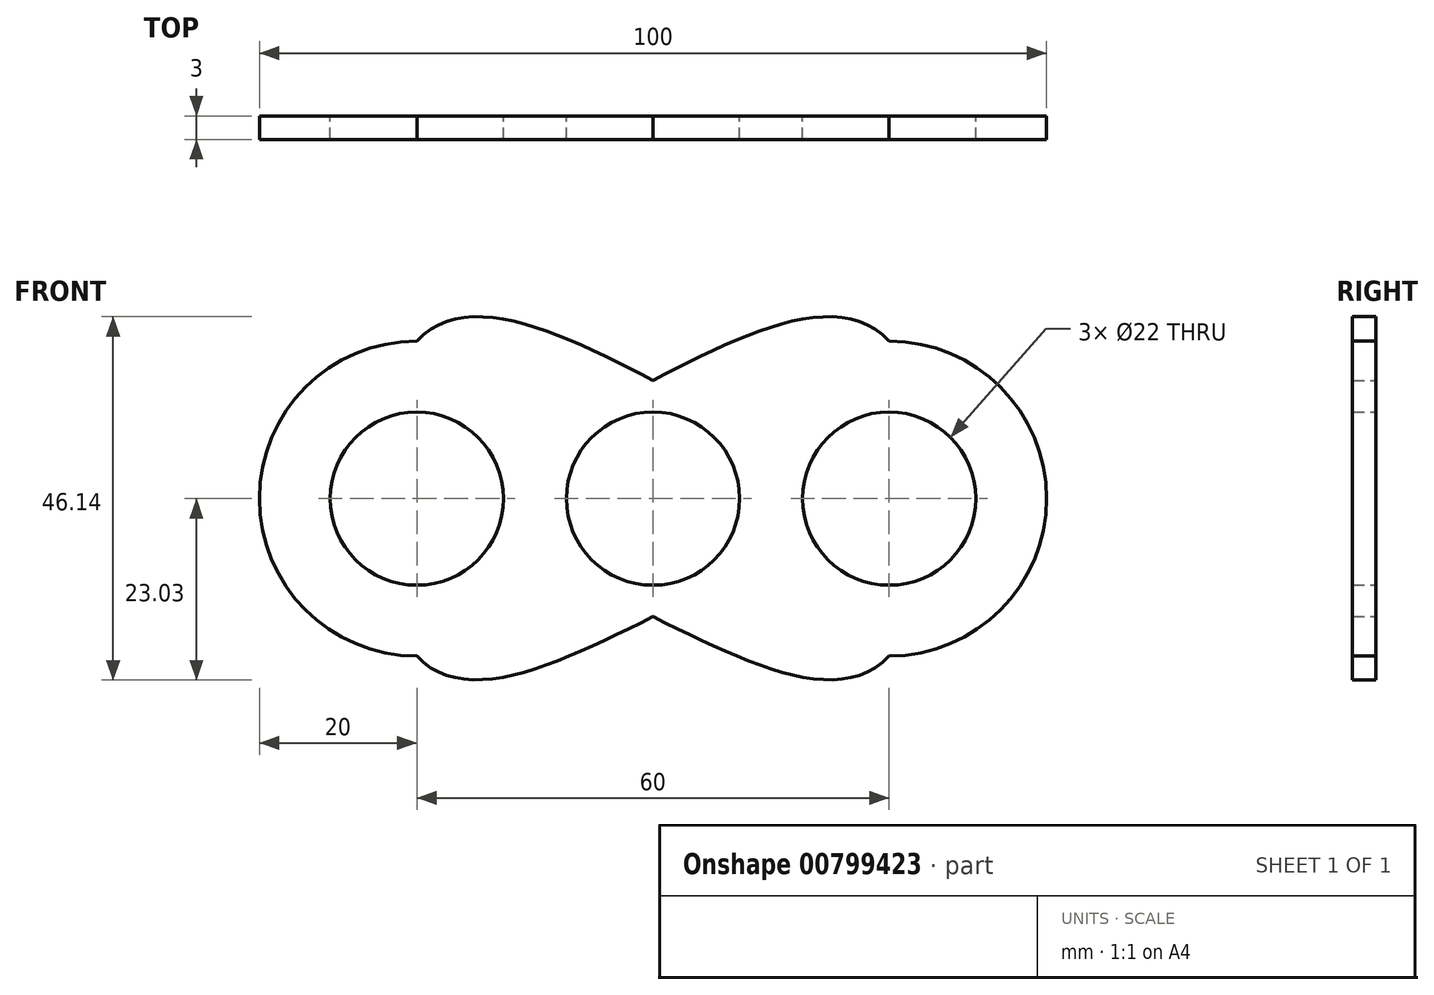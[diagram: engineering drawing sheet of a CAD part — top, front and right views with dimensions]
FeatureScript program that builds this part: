
annotation { "Feature Type Name" : "Feature", "Feature Type Description" : "" }
export const myFeature = defineFeature(function(context is Context, id is Id, definition is map)
    precondition{}
    {
        {
            var Q0;
            Q0=qCreatedBy(makeId("Front.planeOp"),FACE);
            var sketch = newSketch(context, id + "F0", { "sketchPlane" : qUnion([Q0])});
            skCircle(sketch, "E0", {"center": v(0, 0) * mm, "radius": 11 * mm});
            skCircle(sketch, "E1", {"center": v(30, 0) * mm, "radius": 11 * mm});
            skArc(sketch, "E2", {"start": v(0, 15) * mm, "mid": v(-6.77, 13.39) * mm, "end": v(-12.08, 8.89) * mm});
            skArc(sketch, "E3.trimOffspring", {"start": v(12.08, -8.89) * mm, "mid": v(47, -10.54) * mm, "end": v(30, 20) * mm});
            skFitSpline(sketch, "E4", {"points": [v(0, 15) * mm, v(30, 20) * mm, v(30, -20) * mm, v(0, -15) * mm], "startDerivative": vector(110.53, 57.8) * mm, "endDerivative": vector(-111.76, 55.61) * mm});
            skArc(sketch, "E5.MirrorCS", {"start": v(-30, -20) * mm, "mid": v(-47, 10.54) * mm, "end": v(-12.08, 8.89) * mm});
            skCircle(sketch, "E6.MirrorC", {"center": v(-30, 0) * mm, "radius": 11 * mm});
            skFitSpline(sketch, "E7.MirrorCS", {"points": [v(0, 15) * mm, v(-30, 20) * mm, v(-30, -20) * mm, v(0, -15) * mm], "startDerivative": vector(-110.53, 57.8) * mm, "endDerivative": vector(111.76, 55.61) * mm});
            skArc(sketch, "E8.trimOffspring", {"start": v(0, -15) * mm, "mid": v(6.77, -13.39) * mm, "end": v(12.08, -8.89) * mm});
            skPoint(sketch, "E9.orphan", {"position": v(12.08, 8.89) * mm});
            skPoint(sketch, "E10.orphan", {"position": v(-12.08, -8.89) * mm});
            skSolve(sketch);
        }
        {
            var Q0;
            Q0 = qSketchRegion(id + "F0", true);
            extrude(context, id + "F1", {"entities" : qUnion([Q0]), "depth" : 3 * mm, "offsetDistance" : 25 * mm});
        }
    });
